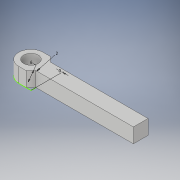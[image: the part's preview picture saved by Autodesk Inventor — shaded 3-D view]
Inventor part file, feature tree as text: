
AUTODESK INVENTOR PART (.ipt)
format: ipt  version: 2019 (Build 230136000, 136)  size: 155,648 bytes
history: native  units: mm
features: extrude x4, sketch x2, chamfer x1
ambient origin geometry x8: Origin, YZ Plane, XZ Plane, XY Plane, X Axis, Y Axis, Z Axis, Center Point
bodies: Solid1 (feature_tree)
feature tree (7):
  sketch  "Sketch1"  dims[d0=6.0mm d1=2.0mm]
  extrude  "Extrusion1"  Depth=2.0mm
  extrude  "Extrusion2"  Depth=6.0mm TaperAngle=0.0deg
  extrude  "Extrusion3"  Depth=6.0mm TaperAngle=0.0deg
  extrude  "Extrusion4"  TaperAngle=0.0deg  [1 undecoded]
  chamfer  "Chamfer1"  Distance=2.0mm
  sketch  "Sketch2"  dims[d2=6.0mm d3=0.0mm d4=6.0mm d5=0.0mm d6=6.0mm d7=0.0mm d8=0.0mm d9=2.0mm d10=2.0mm d11=40.0mm d12=0.0mm d13=2.0mm d14=2.0mm d15=45.0deg]
note: 1 required parameter value undecoded (feature->parameter linkage not recoverable at this tier; creation-order binding heuristic only, values carry confidence <= 0.55)
